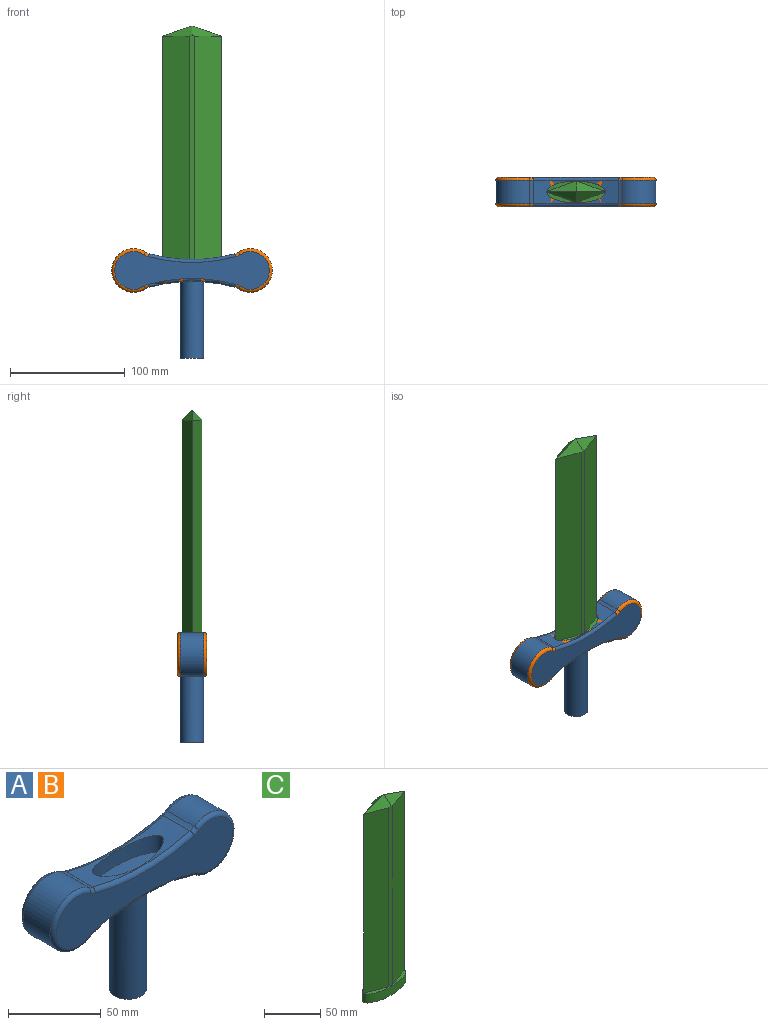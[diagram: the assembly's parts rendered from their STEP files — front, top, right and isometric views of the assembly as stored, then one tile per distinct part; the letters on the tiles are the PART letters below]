
ASSEMBLY  parts=3 mates=1
PART A: 31 faces, bbox 142.8x25.4x96.8 mm
  f0: cylinder r=139.7mm len=37.24mm, axis (0,1,0), area 603.7mm2, adj f7,f14,f22,f27
  f1: cylinder r=11.43mm len=20.32mm, axis (0,1,0), area 71.2mm2, adj f2,f8,f16,f24
  f2: cylinder r=19.05mm len=38.1mm, axis (0,1,0), area 1662.3mm2, adj f1,f3,f18,f26
  f3: cylinder r=11.43mm len=20.32mm, axis (0,1,0), area 71.2mm2, adj f2,f4,f17,f25
  f4: cylinder r=139.7mm len=74.48mm, axis (0,1,0), area 769.3mm2, adj f3,f5,f15,f23,f29
  f5: cylinder r=11.43mm len=20.32mm, axis (0,1,0), area 71.2mm2, adj f4,f6,f13,f21
  f6: cylinder r=19.05mm len=38.1mm, axis (0,1,0), area 1662.3mm2, adj f5,f7,f11,f19
  f7: cylinder r=11.43mm len=20.32mm, axis (0,1,0), area 71.2mm2, adj f0,f6,f12,f20
  f8: cylinder r=139.7mm len=37.24mm, axis (0,1,0), area 603.7mm2, adj f1,f14,f22,f27
  f9: plane 134.62x33.02mm, normal (0,-1,0), area 2931.2mm2, adj f19,f20,f21,f22,f23,f24,f25,f26
  f10: plane 134.62x33.02mm, normal (0,1,0), area 2931.2mm2, adj f11,f12,f13,f14,f15,f16,f17,f18
  f11: torus R=16.51mm, axis (0,-1,0), area 310.6mm2, adj f6,f10,f12,f13
  f12: torus R=13.97mm, axis (0,-1,0), area 15.1mm2, adj f7,f10,f11,f14
  f13: torus R=13.97mm, axis (0,-1,0), area 15.1mm2, adj f5,f10,f11,f15
  f14: torus R=142.24mm, axis (0,-1,0), area 302.8mm2, adj f0,f8,f10,f12,f16
  f15: torus R=142.24mm, axis (0,-1,0), area 302.8mm2, adj f4,f10,f13,f17
  f16: torus R=13.97mm, axis (0,-1,0), area 15.1mm2, adj f1,f10,f14,f18
  f17: torus R=13.97mm, axis (0,-1,0), area 15.1mm2, adj f3,f10,f15,f18
  f18: torus R=16.51mm, axis (0,-1,0), area 310.6mm2, adj f2,f10,f16,f17
  f19: torus R=16.51mm, axis (0,-1,0), area 310.6mm2, adj f6,f9,f20,f21
  f20: torus R=13.97mm, axis (0,-1,0), area 15.1mm2, adj f7,f9,f19,f22
  f21: torus R=13.97mm, axis (0,-1,0), area 15.1mm2, adj f5,f9,f19,f23
  f22: torus R=142.24mm, axis (0,-1,0), area 302.8mm2, adj f0,f8,f9,f20,f24
  f23: torus R=142.24mm, axis (0,-1,0), area 302.8mm2, adj f4,f9,f21,f25
  f24: torus R=13.97mm, axis (0,-1,0), area 15.1mm2, adj f1,f9,f22,f26
  f25: torus R=13.97mm, axis (0,-1,0), area 15.1mm2, adj f3,f9,f23,f26
  f26: torus R=16.51mm, axis (0,-1,0), area 310.6mm2, adj f2,f9,f24,f25
  f27: cylinder r=10.16mm len=66.71mm, axis (0,0,1), area 4247mm2, adj f0,f8,f28
  f28: plane 20.32x20.32mm, normal (0,0,-1), area 324.3mm2, adj f27
  f29: extruded ~50.8x19.05mm, area 1201.6mm2, adj f4,f30
  f30: plane 50.8x19.05mm, normal (0,0,1), area 760.1mm2, adj f29
PART B: same geometry as A
PART C: 15 faces, bbox 50.8x19.1x212.9 mm
  f0: plane 50.8x9.53mm, normal (0,0,1), area 140.2mm2, adj f2,f6,f7,f13
  f1: plane 50.8x9.53mm, normal (0,0,1), area 140.2mm2, adj f2,f4,f5,f14
  f2: extruded ~50.8x19.05mm, area 1114.7mm2, adj f0,f1,f3
  f3: plane 50.8x19.05mm, normal (0,0,-1), area 760.1mm2, adj f2
  f4: plane 194.31x23.02mm, normal (-0.35,-0.94,0), area 4777.5mm2, adj f1,f7,f12,f14
  f5: plane 194.31x23.02mm, normal (0.35,-0.94,0), area 4777.5mm2, adj f1,f6,f10,f14
  f6: plane 194.31x23.02mm, normal (0.35,0.94,0), area 4777.5mm2, adj f0,f5,f9,f13
  f7: plane 194.31x23.02mm, normal (-0.35,0.94,0), area 4777.5mm2, adj f0,f4,f11,f13
  f8: plane 0.16x0.06mm, normal (0,0,1), area 0mm2, adj f9,f10,f11,f12
  f9: plane 25.4x8.89mm, normal (0.25,0.66,0.71), area 169.6mm2, adj f6,f8,f10,f11,f13
  f10: plane 25.4x8.89mm, normal (0.25,-0.66,0.71), area 169.6mm2, adj f5,f8,f9,f12,f14
  f11: plane 25.4x8.89mm, normal (-0.25,0.66,0.71), area 169.6mm2, adj f7,f8,f9,f12,f13
  f12: plane 25.4x8.89mm, normal (-0.25,-0.66,0.71), area 169.6mm2, adj f4,f8,f10,f11,f14
  f13: plane 195.15x4.76mm, normal (0,1,0), area 926.2mm2, adj f0,f6,f7,f9,f11
  f14: plane 195.15x4.76mm, normal (0,-1,0), area 926.2mm2, adj f1,f4,f5,f10,f12
PLACE A t=(-4.18,-41.53,-4.7)mm
PLACE B t=(-4.18,-41.53,-4.7)mm
PLACE C t=(-4.18,-41.53,0.13)mm
MATE fastened C.f3 <-> A.f27  axis (0,0,-1) through (-4.18,-41.53,-4.7)mm
